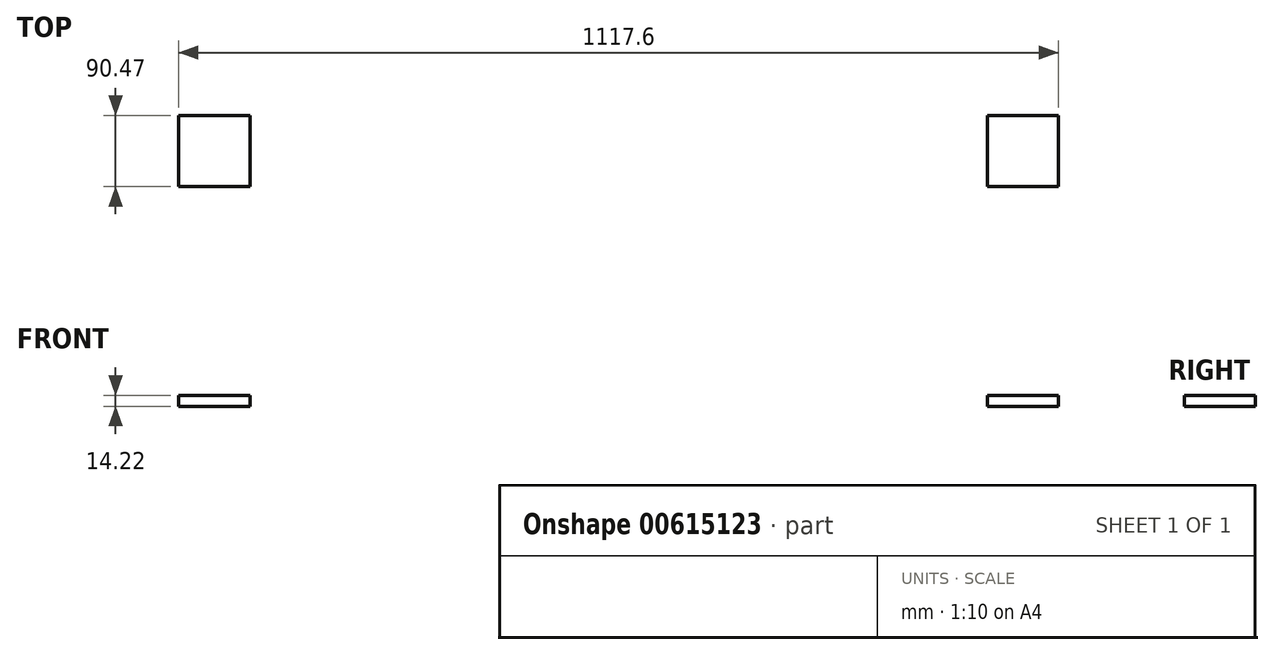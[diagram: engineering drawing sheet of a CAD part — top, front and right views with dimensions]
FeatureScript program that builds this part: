
annotation { "Feature Type Name" : "Feature", "Feature Type Description" : "" }
export const myFeature = defineFeature(function(context is Context, id is Id, definition is map)
    precondition{}
    {
        {
            var Q0;
            Q0=qCreatedBy(makeId("Top.planeOp"),FACE);
            var sketch = newSketch(context, id + "F0", { "sketchPlane" : qUnion([Q0])});
            skLineSegment(sketch, "E0.bottom", {"start": v(-539.36, 469.3) * mm, "end": v(578.24, 469.3) * mm});
            skLineSegment(sketch, "E0.top", {"start": v(-539.36, -397.36) * mm, "end": v(578.24, -397.36) * mm});
            skLineSegment(sketch, "E0.left", {"start": v(-539.36, 469.3) * mm, "end": v(-539.36, -397.36) * mm});
            skLineSegment(sketch, "E0.right", {"start": v(578.24, 469.3) * mm, "end": v(578.24, -397.36) * mm});
            skLineSegment(sketch, "E1.bottom", {"start": v(-539.36, 469.3) * mm, "end": v(-448.89, 469.3) * mm});
            skLineSegment(sketch, "E1.top", {"start": v(-539.36, 378.82) * mm, "end": v(-448.89, 378.82) * mm});
            skLineSegment(sketch, "E1.left", {"start": v(-539.36, 469.3) * mm, "end": v(-539.36, 378.82) * mm});
            skLineSegment(sketch, "E1.right", {"start": v(-448.89, 469.3) * mm, "end": v(-448.89, 378.82) * mm});
            skLineSegment(sketch, "E2.bottom", {"start": v(578.24, 469.3) * mm, "end": v(487.76, 469.3) * mm});
            skLineSegment(sketch, "E2.top", {"start": v(578.24, 378.82) * mm, "end": v(487.76, 378.82) * mm});
            skLineSegment(sketch, "E2.left", {"start": v(578.24, 469.3) * mm, "end": v(578.24, 378.82) * mm});
            skLineSegment(sketch, "E2.right", {"start": v(487.76, 469.3) * mm, "end": v(487.76, 378.82) * mm});
            skLineSegment(sketch, "E3.bottom", {"start": v(578.24, -397.36) * mm, "end": v(487.76, -397.36) * mm});
            skLineSegment(sketch, "E3.top", {"start": v(578.24, -306.88) * mm, "end": v(487.76, -306.88) * mm});
            skLineSegment(sketch, "E3.left", {"start": v(578.24, -397.36) * mm, "end": v(578.24, -306.88) * mm});
            skLineSegment(sketch, "E3.right", {"start": v(487.76, -397.36) * mm, "end": v(487.76, -306.88) * mm});
            skLineSegment(sketch, "E4.bottom", {"start": v(-539.36, -397.36) * mm, "end": v(-448.89, -397.36) * mm});
            skLineSegment(sketch, "E4.top", {"start": v(-539.36, -306.88) * mm, "end": v(-448.89, -306.88) * mm});
            skLineSegment(sketch, "E4.left", {"start": v(-539.36, -397.36) * mm, "end": v(-539.36, -306.88) * mm});
            skLineSegment(sketch, "E4.right", {"start": v(-448.89, -397.36) * mm, "end": v(-448.89, -306.88) * mm});
            skSolve(sketch);
        }
        {
            var Q0;
            Q0=makeQuery(id+"F0.imprint","IMPRINT",FACE,{"disambiguationData":[TD([[makeQuery(id+"F0.imprint","IMPRINT",EDGE,{"derivedFrom":sQuery(id+"F0.wireOp",EDGE,"E0.bottom")}),-1.0]])]});
            extrude(context, id + "F1", {"entities" : qUnion([Q0]), "depth" : 14.22 * mm});
        }
    });
